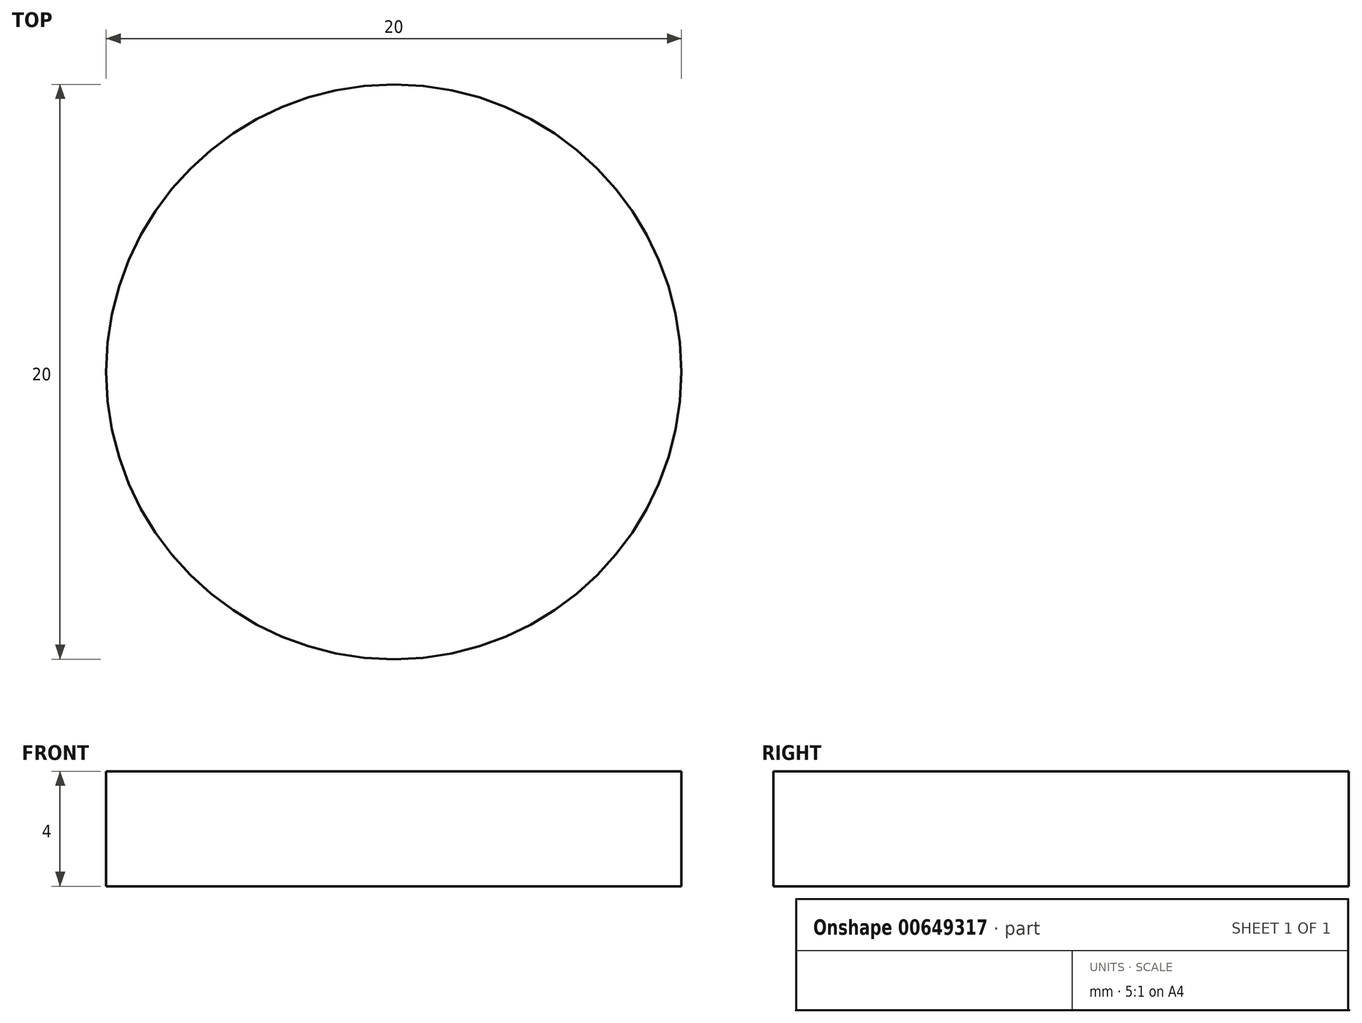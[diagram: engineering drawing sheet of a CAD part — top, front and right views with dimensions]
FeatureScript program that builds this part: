
annotation { "Feature Type Name" : "Feature", "Feature Type Description" : "" }
export const myFeature = defineFeature(function(context is Context, id is Id, definition is map)
    precondition{}
    {
        {
            var Q0;
            Q0=qCreatedBy(makeId("Top.planeOp"),FACE);
            var sketch = newSketch(context, id + "F0", { "sketchPlane" : qUnion([Q0])});
            skCircle(sketch, "E0", {"center": v(0, 5.42) * mm, "radius": 10 * mm});
            skSolve(sketch);
        }
        {
            var Q0;
            Q0=makeQuery(id+"F0.imprint","IMPRINT",FACE,{"disambiguationData":[TD([[makeQuery(id+"F0.imprint","IMPRINT",EDGE,{"derivedFrom":sQuery(id+"F0.wireOp",EDGE,"E0")}),1.0]])]});
            extrude(context, id + "F1", {"entities" : qUnion([Q0]), "depth" : 4 * mm, "offsetDistance" : 25 * mm});
        }
    });
